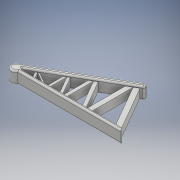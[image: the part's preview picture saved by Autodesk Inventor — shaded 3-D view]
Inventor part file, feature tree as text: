
AUTODESK INVENTOR PART (.ipt)
format: ipt  version: 2018.3 (Build 223284000, 284)  size: 266,240 bytes
history: native  units: mm
features: fillet x3, extrude x2, sketch x2, plane x1
ambient origin geometry x8: Origin, YZ Plane, XZ Plane, XY Plane, X Axis, Y Axis, Z Axis, Center Point
bodies: Solid1 (feature_tree)
feature tree (8):
  extrude  "Extrusion1"  Depth=3.0mm
  fillet  "Fillet1"  Radius=6.0mm
  fillet  "Fillet2"  Radius=15.0mm
  fillet  "Fillet3"  Radius=2.0mm
  plane  "Work Plane1"
  extrude  "Extrusion5"  Depth=2.0mm
  sketch  "Sketch1"  dims[d0=130.0mm d1=3.0mm d2=6.0mm d3=15.0mm d4=0.0mm d5=2.0mm]
  sketch  "Sketch2"  dims[d6=2.0mm d7=2.0mm d8=120.0deg d9=15.0mm d10=30.0deg d15=1.5mm d18=90.0deg d28=3.0mm d29=60.0deg d30=3.0mm d31=90.0deg d32=4.0mm d47=30.0deg d51=60.0deg d52=6.0mm d54=6.0mm d55=4.0mm d56=60.0deg d57=115.0mm d58=10.0mm d59=0.0mm]
